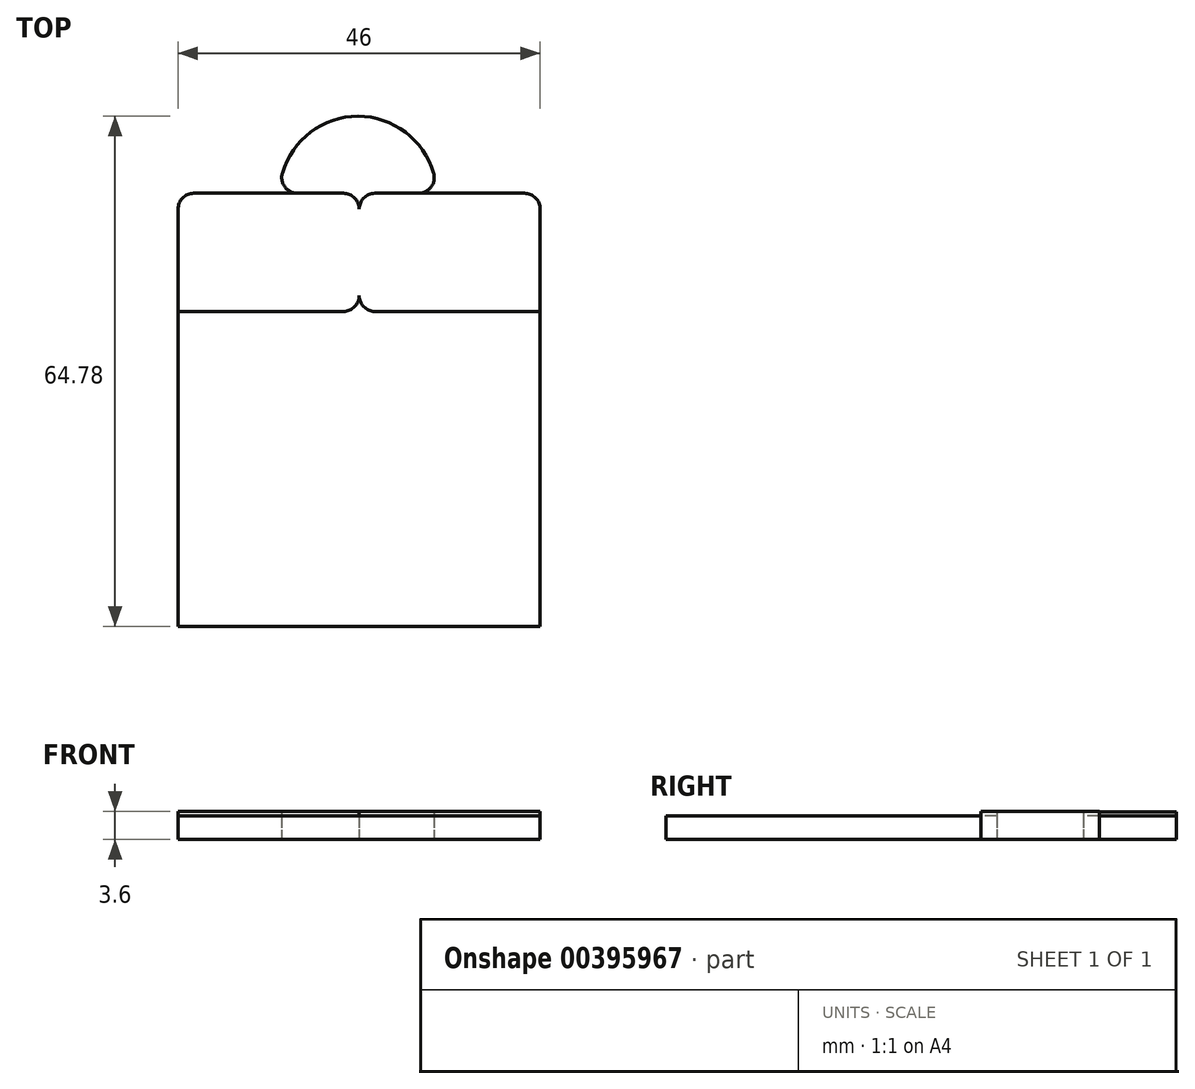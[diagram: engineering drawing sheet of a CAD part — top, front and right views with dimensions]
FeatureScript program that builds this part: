
annotation { "Feature Type Name" : "Feature", "Feature Type Description" : "" }
export const myFeature = defineFeature(function(context is Context, id is Id, definition is map)
    precondition{}
    {
        {
            var Q0;
            Q0=qCreatedBy(makeId("Top.planeOp"),FACE);
            var sketch = newSketch(context, id + "F0", { "sketchPlane" : qUnion([Q0])});
            skLineSegment(sketch, "E0.bottom", {"start": v(0, 0) * mm, "end": v(46, 0) * mm});
            skLineSegment(sketch, "E0.top", {"start": v(25, 55) * mm, "end": v(44, 55) * mm});
            skLineSegment(sketch, "E0.left", {"start": v(0, 0) * mm, "end": v(0, 53) * mm});
            skLineSegment(sketch, "E1.top", {"start": v(43, 40) * mm, "end": v(25, 40) * mm});
            skPoint(sketch, "E1.middle", {"position": v(23, 19.82) * mm});
            skLineSegment(sketch, "E2", {"start": v(0, 40) * mm, "end": v(21, 40) * mm});
            skLineSegment(sketch, "E3", {"start": v(23, 42) * mm, "end": v(23, 53) * mm});
            skLineSegment(sketch, "E4", {"start": v(0, 53) * mm, "end": v(0, 40) * mm});
            skLineSegment(sketch, "E5", {"start": v(2, 55) * mm, "end": v(21, 55) * mm});
            skLineSegment(sketch, "E6", {"start": v(25, 40) * mm, "end": v(46, 40) * mm});
            skLineSegment(sketch, "E7", {"start": v(46, 40) * mm, "end": v(46, 53) * mm});
            skPoint(sketch, "E8.visualSharp", {"position": v(0, 55) * mm});
            skArc(sketch, "E8.filletArc", {"start": v(2, 55) * mm, "mid": v(0.59, 54.41) * mm, "end": v(0, 53) * mm});
            skPoint(sketch, "E9.visualSharp", {"position": v(46, 55) * mm});
            skLineSegment(sketch, "E10", {"start": v(23, 53) * mm, "end": v(23, 42) * mm});
            skLineSegment(sketch, "E11", {"start": v(46, 40) * mm, "end": v(46, 0) * mm});
            skLineSegment(sketch, "E12.bottom", {"start": v(44.01, 3) * mm, "end": v(1.99, 3) * mm});
            skLineSegment(sketch, "E12.top", {"start": v(44.01, 36.63) * mm, "end": v(1.99, 36.63) * mm});
            skLineSegment(sketch, "E12.left", {"start": v(44.01, 3) * mm, "end": v(44.01, 36.63) * mm});
            skLineSegment(sketch, "E12.right", {"start": v(1.99, 3) * mm, "end": v(1.99, 36.63) * mm});
            skArc(sketch, "E13.filletArc", {"start": v(46, 53) * mm, "mid": v(45.41, 54.41) * mm, "end": v(44, 55) * mm});
            skPoint(sketch, "E14.newPointB", {"position": v(23, 55) * mm});
            skArc(sketch, "E14.filletArc", {"start": v(25, 55) * mm, "mid": v(23.59, 54.41) * mm, "end": v(23, 53) * mm});
            skArc(sketch, "E15.filletArc", {"start": v(23, 53) * mm, "mid": v(22.41, 54.41) * mm, "end": v(21, 55) * mm});
            skPoint(sketch, "E16.newPointA", {"position": v(46, 40) * mm});
            skPoint(sketch, "E16.newPointB", {"position": v(23, 40) * mm});
            skArc(sketch, "E16.filletArc", {"start": v(21, 40) * mm, "mid": v(22.41, 40.59) * mm, "end": v(23, 42) * mm});
            skArc(sketch, "E17.filletArc", {"start": v(23, 42) * mm, "mid": v(23.59, 40.59) * mm, "end": v(25, 40) * mm});
            skLineSegment(sketch, "E18.trimOffspring", {"start": v(21, 40) * mm, "end": v(3, 40) * mm});
            skPoint(sketch, "E19.orphan", {"position": v(50, 0) * mm});
            skLineSegment(sketch, "E20", {"start": v(0, 55) * mm, "end": v(9.65, 55) * mm});
            skLineSegment(sketch, "E21", {"start": v(46, 55) * mm, "end": v(36.35, 55) * mm});
            skLineSegment(sketch, "E22", {"start": v(30.54, 55) * mm, "end": v(25, 55) * mm});
            skArc(sketch, "E23", {"start": v(34.37, 56.7) * mm, "mid": v(23, 66.5) * mm, "end": v(11.63, 56.7) * mm});
            skArc(sketch, "E24", {"start": v(32.47, 57.55) * mm, "mid": v(22.85, 64.78) * mm, "end": v(13.24, 57.55) * mm});
            skArc(sketch, "E25.filletArc", {"start": v(13.24, 57.55) * mm, "mid": v(13.57, 55.8) * mm, "end": v(15.17, 55) * mm});
            skArc(sketch, "E26.filletArc", {"start": v(30.54, 55) * mm, "mid": v(32.14, 55.8) * mm, "end": v(32.47, 57.55) * mm});
            skPoint(sketch, "E27.visualSharp", {"position": v(11.5, 55) * mm});
            skArc(sketch, "E27.filletArc", {"start": v(9.65, 55) * mm, "mid": v(10.95, 55.48) * mm, "end": v(11.63, 56.7) * mm});
            skPoint(sketch, "E28.visualSharp", {"position": v(34.5, 55) * mm});
            skArc(sketch, "E28.filletArc", {"start": v(34.37, 56.7) * mm, "mid": v(35.05, 55.48) * mm, "end": v(36.35, 55) * mm});
            skLineSegment(sketch, "E29.trimOffspring", {"start": v(21, 55) * mm, "end": v(15.17, 55) * mm});
            skSolve(sketch);
        }
        {
            var Q0;
            Q0=makeQuery(id+"F0.imprint","IMPRINT",FACE,{"disambiguationData":[TD([[makeQuery(id+"F0.imprint","IMPRINT",EDGE,{"derivedFrom":sQuery(id+"F0.wireOp",EDGE,"E12.bottom")}),-1.0]])]});
            var Q1;
            Q1=makeQuery(id+"F0.imprint","IMPRINT",FACE,{"disambiguationData":[TD([[makeQuery(id+"F0.imprint","IMPRINT",EDGE,{"derivedFrom":sQuery(id+"F0.wireOp",EDGE,"E0.bottom")}),1.0]])]});
            var Q2;
            Q2=makeQuery(id+"F0.imprint","IMPRINT",FACE,{"disambiguationData":[TD([[makeQuery(id+"F0.imprint","IMPRINT",EDGE,{"derivedFrom":sQuery(id+"F0.wireOp",EDGE,"E14.filletArc")}),-1.0]])]});
            var Q3;
            Q3=makeQuery(id+"F0.imprint","IMPRINT",FACE,{"disambiguationData":[TD([[makeQuery(id+"F0.imprint","IMPRINT",EDGE,{"derivedFrom":sQuery(id+"F0.wireOp",EDGE,"E0.top")}),1.0]])]});
            extrude(context, id + "F1", {"entities" : qUnion([Q0, Q1, Q2, Q3]), "depth" : 3 * mm});
        }
        {
            var Q0;
            Q0=makeQuery(id+"F0.imprint","IMPRINT",FACE,{"disambiguationData":[TD([[makeQuery(id+"F0.imprint","IMPRINT",EDGE,{"derivedFrom":sQuery(id+"F0.wireOp",EDGE,"E2")}),1.0]])]});
            var Q1;
            {var subQ4=sQuery(id+"F0.wireOp",EDGE,"E0.top");Q1=makeQuery(id+"F0.imprint","IMPRINT",FACE,{"disambiguationData":[TD([[makeQuery(id+"F0.imprint","IMPRINT",EDGE,{"derivedFrom":subQ4}),-1.0]])]});}
            extrude(context, id + "F2", {"entities" : qUnion([Q0, Q1]), "depth" : 3.6 * mm});
        }
        {
            var Q0;
            Q0=makeQuery(id+"F0.imprint","IMPRINT",FACE,{"disambiguationData":[TD([[makeQuery(id+"F0.imprint","IMPRINT",EDGE,{"derivedFrom":sQuery(id+"F0.wireOp",EDGE,"E14.filletArc")}),-1.0]])]});
            extrude(context, id + "F3", {"entities" : qUnion([Q0]), "depth" : 3.5 * mm});
        }
        {
            var Q0;
            Q0=sQuery(id+"F0.wireOp",EDGE,"E12.right");
            var Q1;
            Q1=sQuery(id+"F0.wireOp",EDGE,"E12.top");
            var Q2;
            Q2=sQuery(id+"F0.wireOp",EDGE,"E12.left");
            var Q3;
            Q3=sQuery(id+"F0.wireOp",EDGE,"E12.bottom");
            extrude(context, id + "F4", {"bodyType" : ToolBodyType.SURFACE, "surfaceEntities" : qUnion([Q0, Q1, Q2, Q3]), "depth" : 3.5 * mm});
        }
    });
